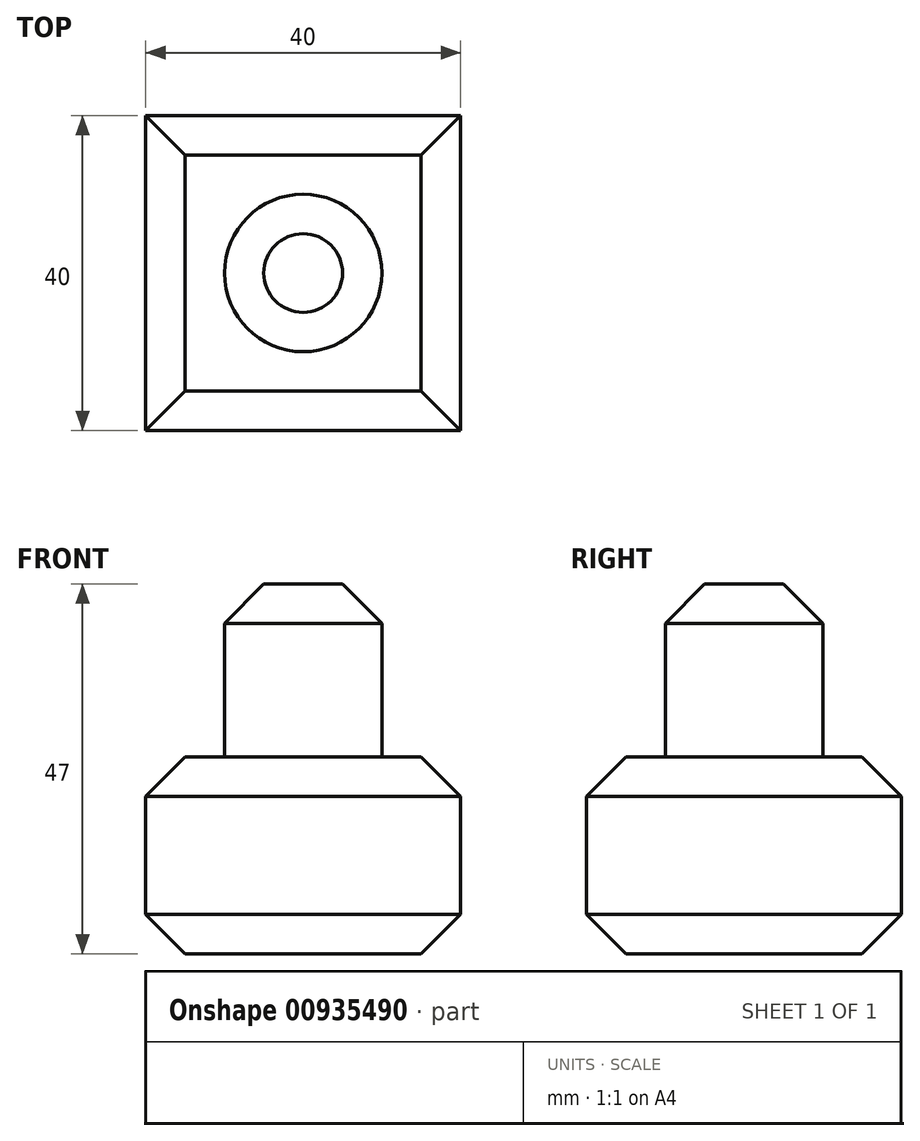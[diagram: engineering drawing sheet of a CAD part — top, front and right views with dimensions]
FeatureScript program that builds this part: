
annotation { "Feature Type Name" : "Feature", "Feature Type Description" : "" }
export const myFeature = defineFeature(function(context is Context, id is Id, definition is map)
    precondition{}
    {
        {
            var Q0;
            Q0=qCreatedBy(makeId("Top.planeOp"),FACE);
            var sketch = newSketch(context, id + "F0", { "sketchPlane" : qUnion([Q0])});
            skLineSegment(sketch, "E0.bottom", {"start": v(20, 20) * mm, "end": v(-20, 20) * mm});
            skLineSegment(sketch, "E0.top", {"start": v(20, -20) * mm, "end": v(-20, -20) * mm});
            skLineSegment(sketch, "E0.left", {"start": v(20, 20) * mm, "end": v(20, -20) * mm});
            skLineSegment(sketch, "E0.right", {"start": v(-20, 20) * mm, "end": v(-20, -20) * mm});
            skPoint(sketch, "E0.middle", {"position": v(0, 0) * mm});
            skCircle(sketch, "E1", {"center": v(0, 0) * mm, "radius": 10 * mm});
            skSolve(sketch);
        }
        {
            var Q0;
            Q0=makeQuery(id+"F0.imprint","IMPRINT",FACE,{"disambiguationData":[TD([[makeQuery(id+"F0.imprint","IMPRINT",EDGE,{"derivedFrom":sQuery(id+"F0.wireOp",EDGE,"E0.bottom")}),1.0]])]});
            extrude(context, id + "F1", {"entities" : qUnion([Q0]), "depth" : 25 * mm, "offsetDistance" : 25 * mm});
        }
        {
            var Q0;
            Q0=makeQuery(id+"F0.imprint","IMPRINT",FACE,{"disambiguationData":[TD([[makeQuery(id+"F0.imprint","IMPRINT",EDGE,{"derivedFrom":sQuery(id+"F0.wireOp",EDGE,"E1")}),1.0]])]});
            extrude(context, id + "F2", {"entities" : qUnion([Q0]), "operationType" : NewBodyOperationType.ADD, "depth" : 47 * mm, "offsetDistance" : 25 * mm});
        }
        {
            var Q0;
            Q0=makeQuery(id+"F1.opExtrude","CAP_EDGE",EDGE,{"disambiguationData":[OSD([sQuery(id+"F0.wireOp",EDGE,"E0.bottom")])],"isStart":false});
            var Q1;
            Q1=makeQuery(id+"F1.opExtrude","CAP_EDGE",EDGE,{"disambiguationData":[OSD([sQuery(id+"F0.wireOp",EDGE,"E0.left")])],"isStart":false});
            var Q2;
            Q2=makeQuery(id+"F1.opExtrude","CAP_EDGE",EDGE,{"disambiguationData":[OSD([sQuery(id+"F0.wireOp",EDGE,"E0.top")])],"isStart":true});
            var Q3;
            Q3=makeQuery(id+"F1.opExtrude","CAP_EDGE",EDGE,{"disambiguationData":[OSD([sQuery(id+"F0.wireOp",EDGE,"E0.left")])],"isStart":true});
            var Q4;
            Q4=makeQuery(id+"F1.opExtrude","CAP_EDGE",EDGE,{"disambiguationData":[OSD([sQuery(id+"F0.wireOp",EDGE,"E0.bottom")])],"isStart":true});
            var Q5;
            Q5=makeQuery(id+"F1.opExtrude","CAP_EDGE",EDGE,{"disambiguationData":[OSD([sQuery(id+"F0.wireOp",EDGE,"E0.right")])],"isStart":true});
            var Q6;
            Q6=makeQuery(id+"F1.opExtrude","CAP_EDGE",EDGE,{"disambiguationData":[OSD([sQuery(id+"F0.wireOp",EDGE,"E0.top")])],"isStart":false});
            var Q7;
            Q7=makeQuery(id+"F1.opExtrude","CAP_EDGE",EDGE,{"disambiguationData":[OSD([sQuery(id+"F0.wireOp",EDGE,"E0.right")])],"isStart":false});
            var Q8;
            Q8=makeQuery(id+"F2.opExtrude","CAP_FACE",FACE,{"disambiguationData":[OSD([sQuery(id+"F0.wireOp",EDGE,"E1")])],"isStart":false});
            var Q9;
            Q9=makeQuery(id+"F2.opExtrude","CAP_EDGE",EDGE,{"disambiguationData":[OSD([sQuery(id+"F0.wireOp",EDGE,"E1")])],"isStart":false});
            chamfer(context, id + "F3", {"entities" : qUnion([Q0, Q1, Q2, Q3, Q4, Q5, Q6, Q7, Q8, Q9]), "width" : 5 * mm, "tangentPropagation" : true});
        }
    });
